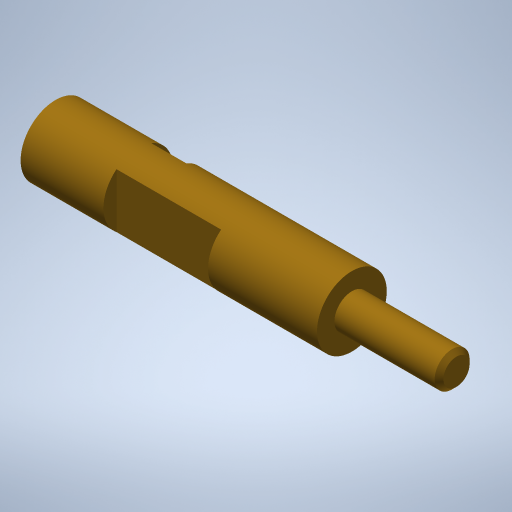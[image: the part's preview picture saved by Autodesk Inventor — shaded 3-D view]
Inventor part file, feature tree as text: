
AUTODESK INVENTOR PART (.ipt)
format: ipt  version: 2024 (Build 280153000, 153)  size: 382,464 bytes
history: native  units: mm (DEFAULTED — no unit token found)
features: other x9, sketch x4, hole x2, plane x2, extrude x2, chamfer x1
ambient origin geometry x1: Ursprung
bodies: Volumenkörper1 (feature_tree)
feature tree (20):
  other  "Grundkörper"
  hole  "3,2 Bohrung axial"  [1 undecoded]
  chamfer  "Fase 0,5x45"  Distance=0.5mm
  plane  "Arbeitsebene1"
  hole  "3,2 Bohrung radial"  [1 undecoded]
  plane  "Arbeitsebene2"
  sketch  "Skizze5"  dims[d4=90.0deg d5=3.2mm d6=6.0mm d7=4.0mm d8=2.0mm d9=14.3117mm d10=14.0mm d11=20.594885mm d12=0.5mm d13=0.5mm d14=11.5mm d15=3.2mm d16=6.0mm d17=4.0mm d18=2.0mm d19=14.3117mm d20=14.0mm d21=20.594885mm d31=1.5mm d32=4.0mm d33=3.2mm d34=5.0mm d35=0.5mm d36=0.5mm d37=4.0mm d38=0.0mm d39=12.0mm d40=0.0mm d41=-9.5mm d42=45.0deg]
  extrude  "Entlüftungssteuerschlitz"  Depth=12.0mm
  extrude  "Belüftungssteuerschlitz"  Depth=4.0mm
  other  "Kurbelwinkel"
  other  "YZ Ebene"
  other  "XZ Ebene"
  other  "XY Ebene"
  other  "X Achse"
  other  "Y Achse"
  other  "Z Achse"
  other  "Mittelpunkt"
  sketch  "Skizze1"  dims[d0=46.0mm d1=12.0mm]
  sketch  "Skizze2"  dims[d2=4.0mm]
  sketch  "Skizze3"  dims[d3=8.0mm]
note: 2 required parameter values undecoded (feature->parameter linkage not recoverable at this tier; creation-order binding heuristic only, values carry confidence <= 0.55)
